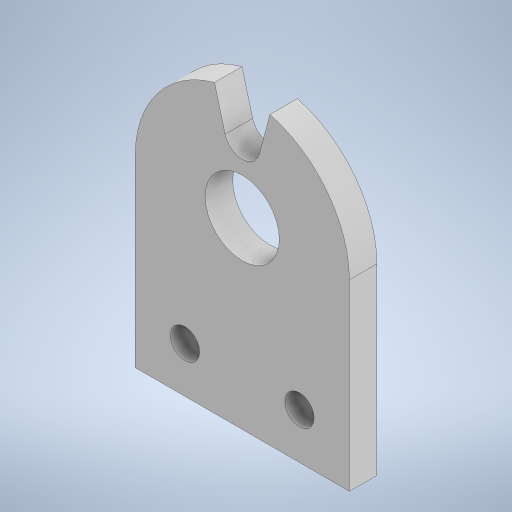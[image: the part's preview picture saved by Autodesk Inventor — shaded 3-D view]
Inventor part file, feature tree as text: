
AUTODESK INVENTOR PART (.ipt)
format: ipt  version: 2023 (Build 270158000, 158)  size: 248,320 bytes
history: native  units: mm
features: extrude x2, sketch x2
ambient origin geometry x8: Origin, YZ Plane, XZ Plane, XY Plane, X Axis, Y Axis, Z Axis, Center Point
bodies: Solid1 (feature_tree)
feature tree (4):
  extrude  "Extrusion1"  Depth=3.0mm TaperAngle=0.0deg
  extrude  "Extrusion2"  Depth=3.0mm
  sketch  "Sketch1"  dims[d0=23.4mm d3=8.1mm d4=20.0mm d6=3.0mm d7=0.0mm]
  sketch  "Sketch2"  dims[d8=30.0deg d9=1.5mm d10=3.2mm d11=5.0mm d12=12.5mm d13=3.0mm d14=0.0mm]
